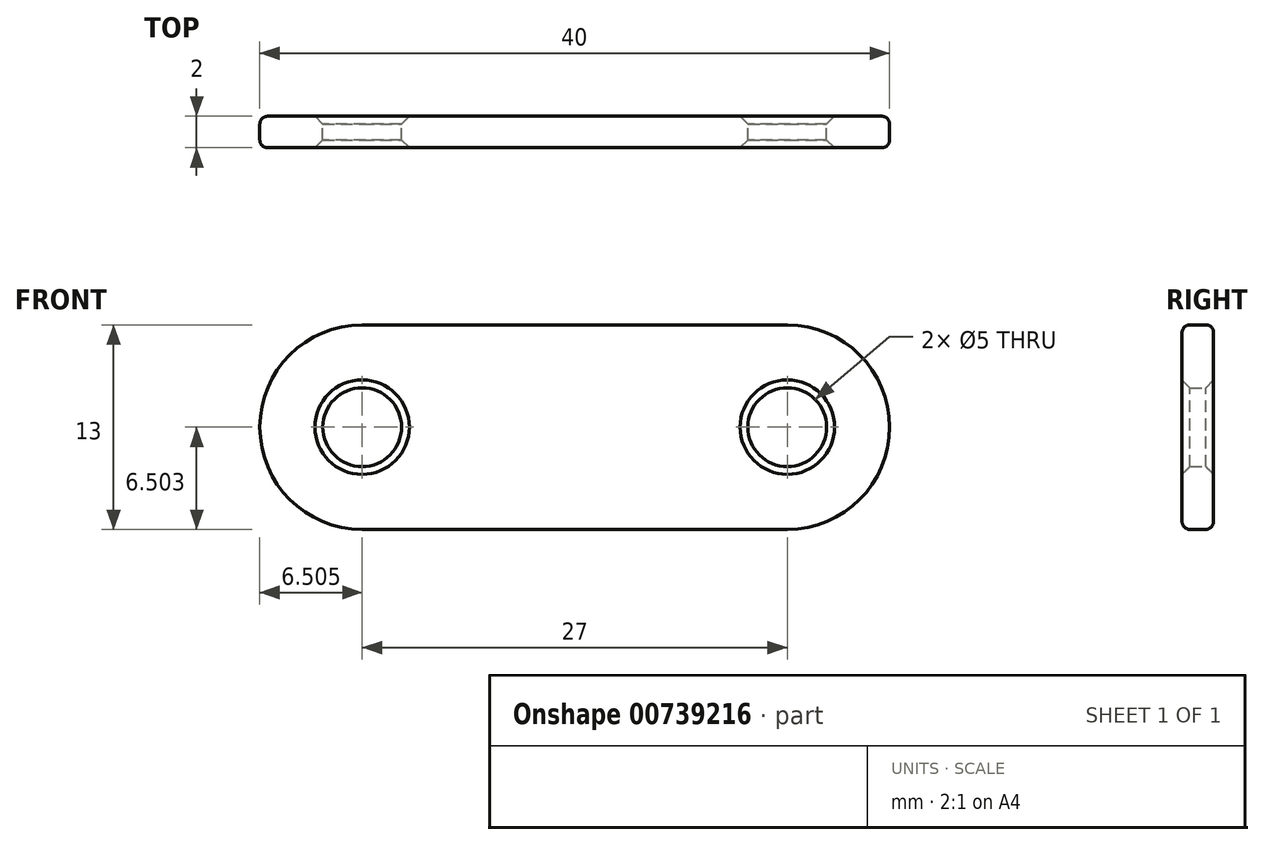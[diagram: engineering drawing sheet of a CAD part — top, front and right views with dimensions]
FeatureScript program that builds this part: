
annotation { "Feature Type Name" : "Feature", "Feature Type Description" : "" }
export const myFeature = defineFeature(function(context is Context, id is Id, definition is map)
    precondition{}
    {
        {
            var Q0;
            Q0=qCreatedBy(makeId("Front.planeOp"),FACE);
            var sketch = newSketch(context, id + "F0", { "sketchPlane" : qUnion([Q0])});
            skLineSegment(sketch, "E0", {"start": v(-16.43, 13.07) * mm, "end": v(10.57, 13.07) * mm});
            skLineSegment(sketch, "E1", {"start": v(-16.43, 0.07) * mm, "end": v(10.57, 0.07) * mm});
            skArc(sketch, "E2", {"start": v(-16.43, 13.07) * mm, "mid": v(-22.93, 6.57) * mm, "end": v(-16.43, 0.07) * mm});
            skArc(sketch, "E3", {"start": v(10.57, 0.07) * mm, "mid": v(17.07, 6.57) * mm, "end": v(10.57, 13.07) * mm});
            skCircle(sketch, "E4", {"center": v(-16.43, 6.57) * mm, "radius": 2.5 * mm});
            skCircle(sketch, "E5", {"center": v(10.57, 6.57) * mm, "radius": 2.5 * mm});
            skSolve(sketch);
        }
        {
            var Q0;
            Q0 = qSketchRegion(id + "F0", true);
            extrude(context, id + "F1", {"entities" : qUnion([Q0]), "depth" : 2 * mm, "offsetDistance" : 25.4 * mm});
        }
        {
            var Q0;
            Q0=makeQuery(id+"F1.opExtrude","CAP_EDGE",EDGE,{"disambiguationData":[OSD([sQuery(id+"F0.wireOp",EDGE,"E2")])],"isStart":false});
            var Q1;
            Q1=makeQuery(id+"F1.opExtrude","CAP_EDGE",EDGE,{"disambiguationData":[OSD([sQuery(id+"F0.wireOp",EDGE,"E1")])],"isStart":true});
            fillet(context, id + "F2", {"entities" : qUnion([Q0, Q1]), "radius" : 0.5 * mm, "tangentPropagation" : true, "allowEdgeOverflow" : false});
        }
        {
            var Q0;
            Q0=makeQuery(id+"F1.opExtrude","CAP_EDGE",EDGE,{"disambiguationData":[OSD([sQuery(id+"F0.wireOp",EDGE,"E4")])],"isStart":false});
            var Q1;
            Q1=makeQuery(id+"F1.opExtrude","CAP_EDGE",EDGE,{"disambiguationData":[OSD([sQuery(id+"F0.wireOp",EDGE,"E5")])],"isStart":true});
            var Q2;
            Q2=makeQuery(id+"F1.opExtrude","CAP_EDGE",EDGE,{"disambiguationData":[OSD([sQuery(id+"F0.wireOp",EDGE,"E5")])],"isStart":false});
            var Q3;
            {var subQ0=sQuery(id+"F0.wireOp",EDGE,"E0");Q3=makeQuery(id+"F2.opFillet","BLEND_EDGE",EDGE,{"blendedFrom":[makeQuery(id+"F1.opExtrude","CAP_EDGE",EDGE,{"disambiguationData":[OSD([subQ0])],"isStart":true}),makeQuery(id+"F1.opExtrude","SWEPT_FACE",FACE,{"disambiguationData":[OSD([subQ0])]})],"blendedInto":[makeQuery(id+"F1.opExtrude","SWEPT_FACE",FACE,{"disambiguationData":[OSD([subQ0])]})]});}
            var Q4;
            Q4=makeQuery(id+"F1.opExtrude","CAP_EDGE",EDGE,{"disambiguationData":[OSD([sQuery(id+"F0.wireOp",EDGE,"E4")])],"isStart":true});
            chamfer(context, id + "F3", {"entities" : qUnion([Q0, Q1, Q2, Q3, Q4]), "width" : 0.5 * mm, "tangentPropagation" : true});
        }
    });
